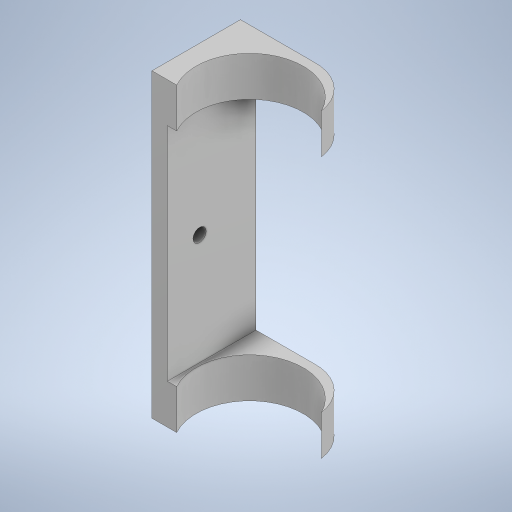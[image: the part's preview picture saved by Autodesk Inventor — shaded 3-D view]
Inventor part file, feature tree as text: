
AUTODESK INVENTOR PART (.ipt)
format: ipt  version: 2024 (Build 280153000, 153)  size: 319,488 bytes
history: native  units: in
note: dims shown in document units (in); Inventor stores cm internally (conversion verified against a paired STEP export)
features: extrude x6, sketch x6, plane x2, mirror x1
ambient origin geometry x8: Origin, YZ Plane, XZ Plane, XY Plane, X Axis, Y Axis, Z Axis, Center Point
bodies: Solid3 (feature_tree)
feature tree (15):
  plane  "Work Plane1"
  extrude  "Extrusion1"  Depth=0.3937in TaperAngle=0.0deg
  plane  "Work Plane4"
  extrude  "Extrusion2"  Depth=0.4085in TaperAngle=0.0deg
  mirror  "Mirror3"
  extrude  "Extrusion3"  Depth=0.0394in TaperAngle=0.0deg
  extrude  "Extrusion4"  Depth=0.0394in
  extrude  "Extrusion5"  [1 undecoded]
  extrude  "Extrusion6"  [1 undecoded]
  sketch  "Sketch2"  dims[d0=0.3937in d1=0.0in d2=0.2165in d3=0.0in]
  sketch  "Sketch3"  dims[d4=0.1181in d5=0.4085in d6=0.0in]
  sketch  "Sketch4"  dims[d7=0.0787in d8=0.0in d9=0.0394in d10=0.0in]
  sketch  "Sketch5"  dims[d11=0.0394in d12=0.0in d13=0.0197in]
  sketch  "Sketch7"  dims[d14=1.9685in]
  sketch  "Sketch8"
note: 2 required parameter values undecoded (feature->parameter linkage not recoverable at this tier; creation-order binding heuristic only, values carry confidence <= 0.55)
